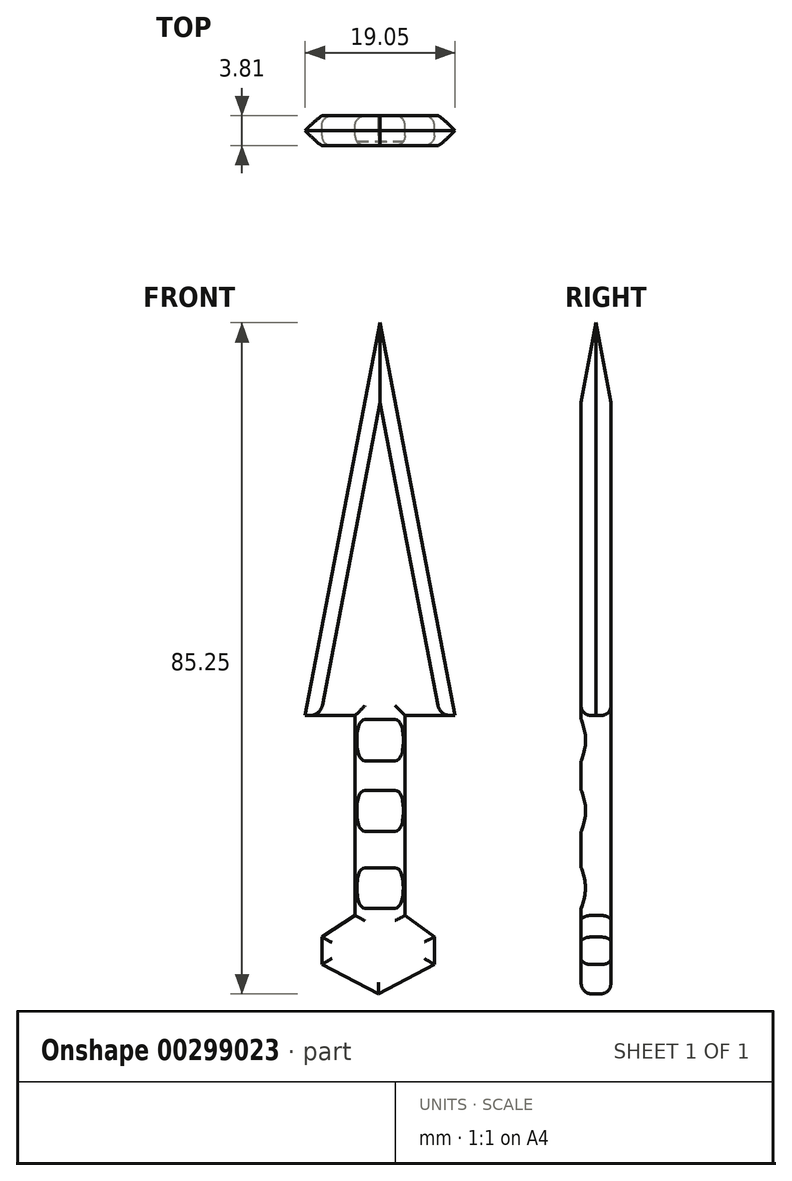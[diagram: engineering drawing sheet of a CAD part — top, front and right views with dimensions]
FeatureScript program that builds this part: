
annotation { "Feature Type Name" : "Feature", "Feature Type Description" : "" }
export const myFeature = defineFeature(function(context is Context, id is Id, definition is map)
    precondition{}
    {
        {
            var Q0;
            Q0=qCreatedBy(makeId("Front.planeOp"),FACE);
            var sketch = newSketch(context, id + "F0", { "sketchPlane" : qUnion([Q0])});
            skLineSegment(sketch, "E0", {"start": v(-12.17, -8.52) * mm, "end": v(-12.17, 16.88) * mm});
            skLineSegment(sketch, "E1", {"start": v(-5.82, -8.52) * mm, "end": v(-5.82, 16.88) * mm});
            skLineSegment(sketch, "E2", {"start": v(-12.17, 16.88) * mm, "end": v(-18.52, 16.88) * mm});
            skLineSegment(sketch, "E3", {"start": v(-18.52, 16.88) * mm, "end": v(-9, 66.78) * mm});
            skLineSegment(sketch, "E4", {"start": v(-5.82, 16.88) * mm, "end": v(0.53, 16.88) * mm});
            skLineSegment(sketch, "E5", {"start": v(0.53, 16.88) * mm, "end": v(-9, 66.78) * mm});
            skLineSegment(sketch, "E6", {"start": v(-12.17, -8.52) * mm, "end": v(-16.4, -11.26) * mm});
            skLineSegment(sketch, "E7", {"start": v(-16.4, -11.26) * mm, "end": v(-16.4, -14.74) * mm});
            skLineSegment(sketch, "E8", {"start": v(-16.4, -14.74) * mm, "end": v(-9.2, -18.47) * mm});
            skLineSegment(sketch, "E9", {"start": v(-9.2, -18.47) * mm, "end": v(-2.1, -14.74) * mm});
            skLineSegment(sketch, "E10", {"start": v(-2.1, -14.74) * mm, "end": v(-2.1, -11.26) * mm});
            skLineSegment(sketch, "E11", {"start": v(-2.1, -11.26) * mm, "end": v(-5.82, -8.52) * mm});
            skSolve(sketch);
        }
        {
            var Q0;
            Q0 = qSketchRegion(id + "F0", true);
            extrude(context, id + "F1", {"entities" : qUnion([Q0]), "depth" : 3.8 * mm});
        }
        {
            var Q0;
            Q0=makeQuery(id+"F1.opExtrude","CAP_EDGE",EDGE,{"disambiguationData":[OSD([sQuery(id+"F0.wireOp",EDGE,"E3")])],"isStart":false});
            var Q1;
            Q1=makeQuery(id+"F1.opExtrude","CAP_EDGE",EDGE,{"disambiguationData":[OSD([sQuery(id+"F0.wireOp",EDGE,"E5")])],"isStart":false});
            var Q2;
            Q2=makeQuery(id+"F1.opExtrude","CAP_EDGE",EDGE,{"disambiguationData":[OSD([sQuery(id+"F0.wireOp",EDGE,"E3")])],"isStart":true});
            var Q3;
            Q3=makeQuery(id+"F1.opExtrude","CAP_EDGE",EDGE,{"disambiguationData":[OSD([sQuery(id+"F0.wireOp",EDGE,"E5")])],"isStart":true});
            chamfer(context, id + "F2", {"entities" : qUnion([Q0, Q1, Q2, Q3]), "width" : 1.9 * mm, "tangentPropagation" : true});
        }
        {
            var Q0;
            Q0=makeQuery(id+"F1.opExtrude","CAP_EDGE",EDGE,{"disambiguationData":[OSD([sQuery(id+"F0.wireOp",EDGE,"E0")])],"isStart":false});
            var Q1;
            Q1=makeQuery(id+"F1.opExtrude","CAP_EDGE",EDGE,{"disambiguationData":[OSD([sQuery(id+"F0.wireOp",EDGE,"E1")])],"isStart":false});
            var Q2;
            Q2=makeQuery(id+"F1.opExtrude","CAP_EDGE",EDGE,{"disambiguationData":[OSD([sQuery(id+"F0.wireOp",EDGE,"E0")])],"isStart":true});
            var Q3;
            Q3=makeQuery(id+"F1.opExtrude","CAP_EDGE",EDGE,{"disambiguationData":[OSD([sQuery(id+"F0.wireOp",EDGE,"E1")])],"isStart":true});
            var Q4;
            Q4=makeQuery(id+"F1.opExtrude","CAP_EDGE",EDGE,{"disambiguationData":[OSD([sQuery(id+"F0.wireOp",EDGE,"E2")])],"isStart":false});
            var Q5;
            Q5=makeQuery(id+"F1.opExtrude","CAP_EDGE",EDGE,{"disambiguationData":[OSD([sQuery(id+"F0.wireOp",EDGE,"E4")])],"isStart":true});
            var Q6;
            Q6=makeQuery(id+"F1.opExtrude","CAP_EDGE",EDGE,{"disambiguationData":[OSD([sQuery(id+"F0.wireOp",EDGE,"E4")])],"isStart":false});
            var Q7;
            Q7=makeQuery(id+"F1.opExtrude","CAP_EDGE",EDGE,{"disambiguationData":[OSD([sQuery(id+"F0.wireOp",EDGE,"E2")])],"isStart":true});
            var Q8;
            Q8=makeQuery(id+"F1.opExtrude","CAP_EDGE",EDGE,{"disambiguationData":[OSD([sQuery(id+"F0.wireOp",EDGE,"yz9ELkfz-Ur0V-gWK1-WHKG-f7WYfZHVGZ1D")])],"isStart":false});
            var Q9;
            Q9=makeQuery(id+"F1.opExtrude","SWEPT_EDGE",EDGE,{"disambiguationData":[OSD([sQuery(id+"F0.wireOp",EDGE,"yz9ELkfz-Ur0V-gWK1-WHKG-f7WYfZHVGZ1D"),sQuery(id+"F0.wireOp",EDGE,"6ac4Uwei-VJuL-rtgo-6ysk-64Q7eSJeDvao")])]});
            var Q10;
            Q10=makeQuery(id+"F1.opExtrude","CAP_EDGE",EDGE,{"disambiguationData":[OSD([sQuery(id+"F0.wireOp",EDGE,"yz9ELkfz-Ur0V-gWK1-WHKG-f7WYfZHVGZ1D")])],"isStart":true});
            var Q11;
            Q11=makeQuery(id+"F1.opExtrude","SWEPT_EDGE",EDGE,{"disambiguationData":[OSD([sQuery(id+"F0.wireOp",EDGE,"6ac4Uwei-VJuL-rtgo-6ysk-64Q7eSJeDvao"),sQuery(id+"F0.wireOp",EDGE,"OsMeEmrF-FKuc-FBuv-2pJ7-iUZ2CorzZWJp")])]});
            var Q12;
            Q12=makeQuery(id+"F1.opExtrude","CAP_EDGE",EDGE,{"disambiguationData":[OSD([sQuery(id+"F0.wireOp",EDGE,"6ac4Uwei-VJuL-rtgo-6ysk-64Q7eSJeDvao")])],"isStart":false});
            var Q13;
            Q13=makeQuery(id+"F1.opExtrude","CAP_EDGE",EDGE,{"disambiguationData":[OSD([sQuery(id+"F0.wireOp",EDGE,"6ac4Uwei-VJuL-rtgo-6ysk-64Q7eSJeDvao")])],"isStart":true});
            var Q14;
            Q14=makeQuery(id+"F1.opExtrude","CAP_EDGE",EDGE,{"disambiguationData":[OSD([sQuery(id+"F0.wireOp",EDGE,"OsMeEmrF-FKuc-FBuv-2pJ7-iUZ2CorzZWJp")])],"isStart":false});
            var Q15;
            Q15=makeQuery(id+"F1.opExtrude","CAP_EDGE",EDGE,{"disambiguationData":[OSD([sQuery(id+"F0.wireOp",EDGE,"Z0wIlIe5-K8ic-EuZ0-4LCc-ydnpgAEdqaLE")])],"isStart":false});
            var Q16;
            Q16=makeQuery(id+"F1.opExtrude","CAP_EDGE",EDGE,{"disambiguationData":[OSD([sQuery(id+"F0.wireOp",EDGE,"Sy4y65qU-Ux9M-PiJL-2dGM-iehzGRjnZ0c9")])],"isStart":false});
            var Q17;
            Q17=makeQuery(id+"F1.opExtrude","SWEPT_EDGE",EDGE,{"disambiguationData":[OSD([sQuery(id+"F0.wireOp",EDGE,"Z0wIlIe5-K8ic-EuZ0-4LCc-ydnpgAEdqaLE"),sQuery(id+"F0.wireOp",EDGE,"Sy4y65qU-Ux9M-PiJL-2dGM-iehzGRjnZ0c9")])]});
            var Q18;
            Q18=makeQuery(id+"F1.opExtrude","CAP_EDGE",EDGE,{"disambiguationData":[OSD([sQuery(id+"F0.wireOp",EDGE,"Sy4y65qU-Ux9M-PiJL-2dGM-iehzGRjnZ0c9")])],"isStart":true});
            var Q19;
            Q19=makeQuery(id+"F1.opExtrude","CAP_EDGE",EDGE,{"disambiguationData":[OSD([sQuery(id+"F0.wireOp",EDGE,"E6")])],"isStart":false});
            var Q20;
            Q20=makeQuery(id+"F1.opExtrude","CAP_EDGE",EDGE,{"disambiguationData":[OSD([sQuery(id+"F0.wireOp",EDGE,"E7")])],"isStart":false});
            var Q21;
            Q21=makeQuery(id+"F1.opExtrude","CAP_EDGE",EDGE,{"disambiguationData":[OSD([sQuery(id+"F0.wireOp",EDGE,"E8")])],"isStart":false});
            var Q22;
            Q22=makeQuery(id+"F1.opExtrude","CAP_EDGE",EDGE,{"disambiguationData":[OSD([sQuery(id+"F0.wireOp",EDGE,"E9")])],"isStart":false});
            var Q23;
            Q23=makeQuery(id+"F1.opExtrude","CAP_EDGE",EDGE,{"disambiguationData":[OSD([sQuery(id+"F0.wireOp",EDGE,"E10")])],"isStart":false});
            var Q24;
            Q24=makeQuery(id+"F1.opExtrude","CAP_EDGE",EDGE,{"disambiguationData":[OSD([sQuery(id+"F0.wireOp",EDGE,"E11")])],"isStart":false});
            var Q25;
            Q25=makeQuery(id+"F1.opExtrude","CAP_EDGE",EDGE,{"disambiguationData":[OSD([sQuery(id+"F0.wireOp",EDGE,"E6")])],"isStart":true});
            var Q26;
            Q26=makeQuery(id+"F1.opExtrude","CAP_EDGE",EDGE,{"disambiguationData":[OSD([sQuery(id+"F0.wireOp",EDGE,"E11")])],"isStart":true});
            var Q27;
            Q27=makeQuery(id+"F1.opExtrude","CAP_EDGE",EDGE,{"disambiguationData":[OSD([sQuery(id+"F0.wireOp",EDGE,"E10")])],"isStart":true});
            var Q28;
            Q28=makeQuery(id+"F1.opExtrude","CAP_EDGE",EDGE,{"disambiguationData":[OSD([sQuery(id+"F0.wireOp",EDGE,"E9")])],"isStart":true});
            var Q29;
            Q29=makeQuery(id+"F1.opExtrude","CAP_EDGE",EDGE,{"disambiguationData":[OSD([sQuery(id+"F0.wireOp",EDGE,"E8")])],"isStart":true});
            var Q30;
            Q30=makeQuery(id+"F1.opExtrude","CAP_EDGE",EDGE,{"disambiguationData":[OSD([sQuery(id+"F0.wireOp",EDGE,"E7")])],"isStart":true});
            fillet(context, id + "F3", {"entities" : qUnion([Q0, Q1, Q2, Q3, Q4, Q5, Q6, Q7, Q8, Q9, Q10, Q11, Q12, Q13, Q14, Q15, Q16, Q17, Q18, Q19, Q20, Q21, Q22, Q23, Q24, Q25, Q26, Q27, Q28, Q29, Q30]), "radius" : 1.27 * mm, "tangentPropagation" : true, "allowEdgeOverflow" : false});
        }
        {
            var Q0;
            Q0=qCreatedBy(makeId("Right.planeOp"),FACE);
            var sketch = newSketch(context, id + "F4", { "sketchPlane" : qUnion([Q0])});
            skCircle(sketch, "E12", {"center": v(-9.6, 13.75) * mm, "radius": 6.35 * mm});
            skCircle(sketch, "E13", {"center": v(-9.62, -5.02) * mm, "radius": 6.35 * mm});
            skCircle(sketch, "E14", {"center": v(-9.6, 4.79) * mm, "radius": 6.35 * mm});
            skSolve(sketch);
        }
        {
            var Q0;
            Q0 = qSketchRegion(id + "F4", true);
            extrude(context, id + "F5", {"entities" : qUnion([Q0]), "operationType" : NewBodyOperationType.REMOVE, "oppositeDirection" : true, "depth" : 25.4 * mm});
        }
    });
